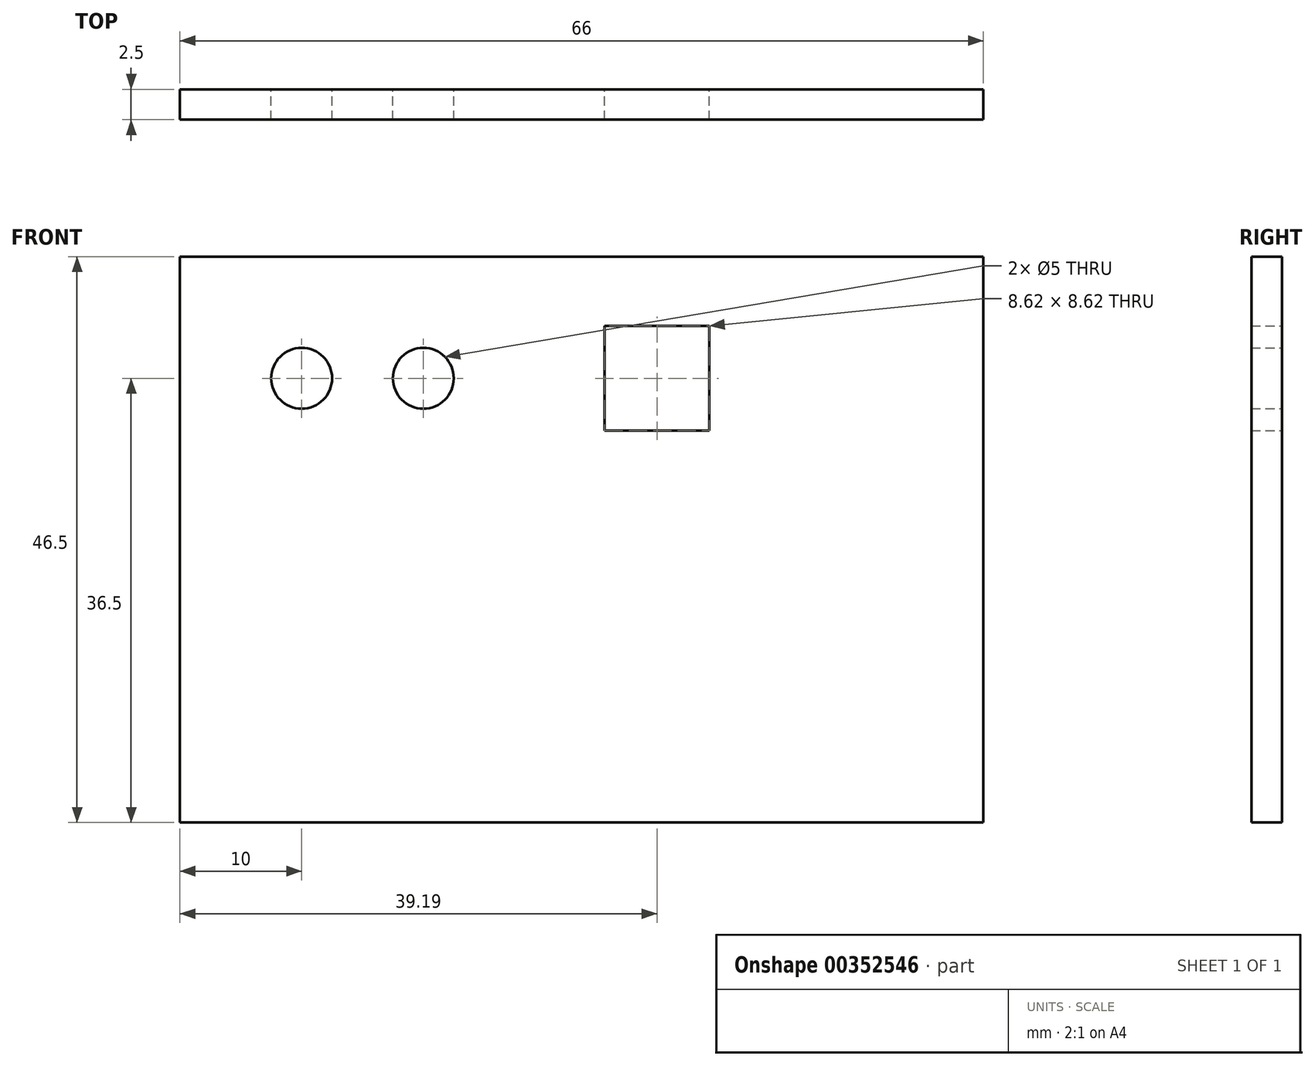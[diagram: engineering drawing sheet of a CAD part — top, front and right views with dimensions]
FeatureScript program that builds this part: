
annotation { "Feature Type Name" : "Feature", "Feature Type Description" : "" }
export const myFeature = defineFeature(function(context is Context, id is Id, definition is map)
    precondition{}
    {
        {
            var Q0;
            Q0=qCreatedBy(makeId("Front.planeOp"),FACE);
            var sketch = newSketch(context, id + "F0", { "sketchPlane" : qUnion([Q0])});
            skLineSegment(sketch, "E0.bottom", {"start": v(0, 0) * mm, "end": v(72, 0) * mm, "construction": true});
            skLineSegment(sketch, "E0.top", {"start": v(0, 52.5) * mm, "end": v(72, 52.5) * mm, "construction": true});
            skLineSegment(sketch, "E0.left", {"start": v(0, 0) * mm, "end": v(0, 52.5) * mm, "construction": true});
            skLineSegment(sketch, "E0.right", {"start": v(72, 0) * mm, "end": v(72, 52.5) * mm, "construction": true});
            skCircle(sketch, "E1", {"center": v(13, 39.5) * mm, "radius": 2.5 * mm});
            skLineSegment(sketch, "E2.bottom", {"start": v(38.38, 35.7) * mm, "end": v(46, 35.7) * mm, "construction": true});
            skLineSegment(sketch, "E2.top", {"start": v(38.38, 43.31) * mm, "end": v(46, 43.31) * mm, "construction": true});
            skLineSegment(sketch, "E2.left", {"start": v(38.38, 35.7) * mm, "end": v(38.38, 43.31) * mm, "construction": true});
            skLineSegment(sketch, "E2.right", {"start": v(46, 35.7) * mm, "end": v(46, 43.31) * mm, "construction": true});
            skLineSegment(sketch, "E3.0", {"start": v(37.88, 35.2) * mm, "end": v(37.88, 43.81) * mm});
            skLineSegment(sketch, "E3.1", {"start": v(37.88, 35.2) * mm, "end": v(46.5, 35.2) * mm});
            skLineSegment(sketch, "E3.2", {"start": v(46.5, 35.2) * mm, "end": v(46.5, 43.81) * mm});
            skLineSegment(sketch, "E3.3", {"start": v(37.88, 43.81) * mm, "end": v(46.5, 43.81) * mm});
            skLineSegment(sketch, "E4.0", {"start": v(3, 3) * mm, "end": v(3, 49.5) * mm});
            skLineSegment(sketch, "E4.1", {"start": v(3, 3) * mm, "end": v(69, 3) * mm});
            skLineSegment(sketch, "E4.2", {"start": v(69, 3) * mm, "end": v(69, 49.5) * mm});
            skLineSegment(sketch, "E4.3", {"start": v(3, 49.5) * mm, "end": v(69, 49.5) * mm});
            skLineSegment(sketch, "E5", {"start": v(38.38, 39.5) * mm, "end": v(46, 39.5) * mm, "construction": true});
            skCircle(sketch, "E6", {"center": v(23, 39.5) * mm, "radius": 2.5 * mm});
            skSolve(sketch);
        }
        {
            var Q0;
            Q0=qSketchRegion(id+"F0",true);
            extrude(context, id + "F1", {"entities" : qUnion([Q0]), "depth" : 2.5 * mm});
        }
    });
